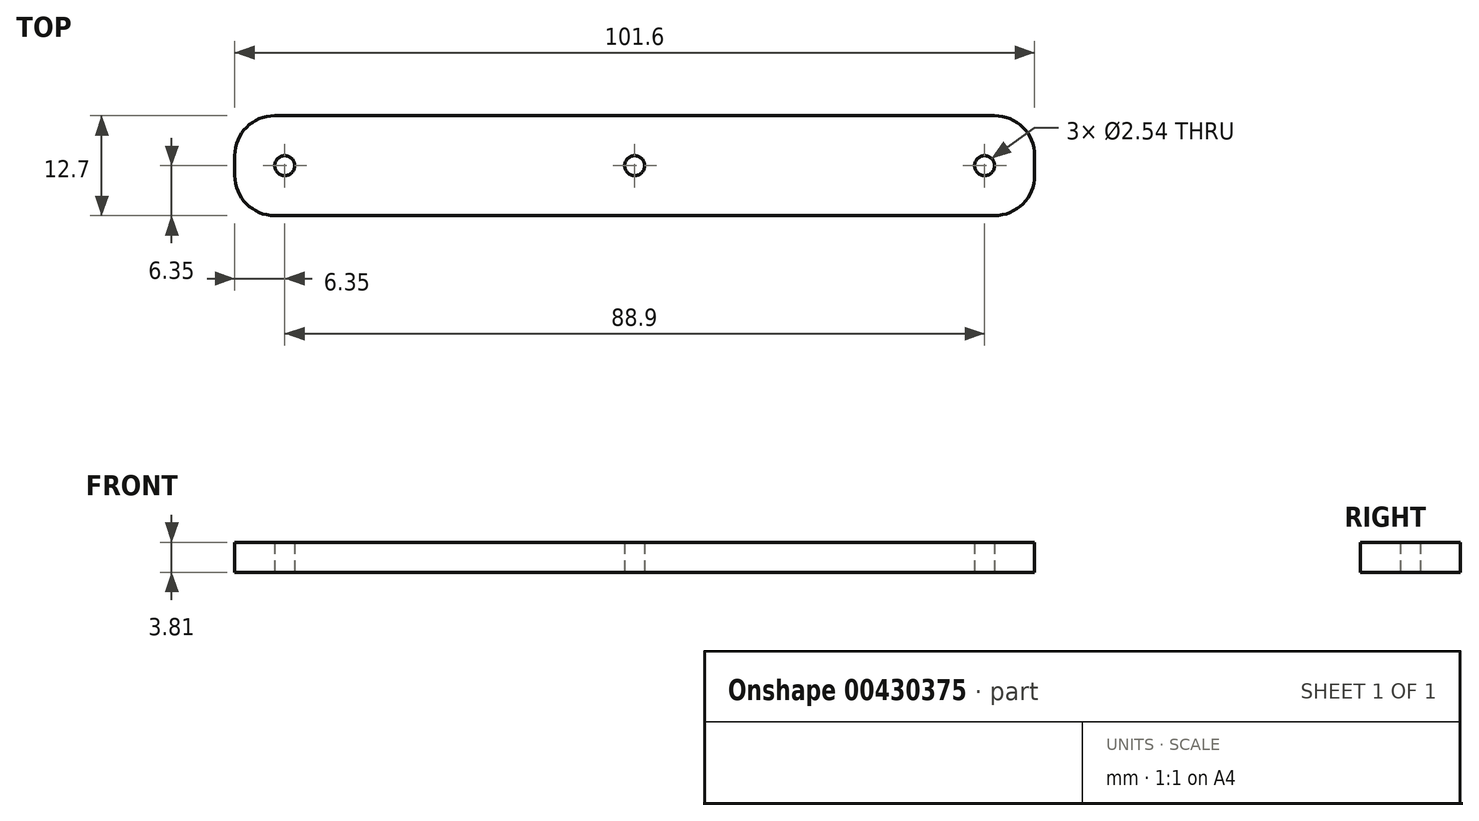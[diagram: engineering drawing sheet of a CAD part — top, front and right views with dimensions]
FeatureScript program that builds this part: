
annotation { "Feature Type Name" : "Feature", "Feature Type Description" : "" }
export const myFeature = defineFeature(function(context is Context, id is Id, definition is map)
    precondition{}
    {
        {
            var Q0;
            Q0=qCreatedBy(makeId("Top.planeOp"),FACE);
            var sketch = newSketch(context, id + "F0", { "sketchPlane" : qUnion([Q0])});
            skLineSegment(sketch, "E0.bottom", {"start": v(0, 0) * mm, "end": v(-101.6, 0) * mm});
            skLineSegment(sketch, "E0.top", {"start": v(0, 12.7) * mm, "end": v(-101.6, 12.7) * mm});
            skLineSegment(sketch, "E0.left", {"start": v(0, 0) * mm, "end": v(0, 12.7) * mm});
            skLineSegment(sketch, "E0.right", {"start": v(-101.6, 0) * mm, "end": v(-101.6, 12.7) * mm});
            skCircle(sketch, "E1", {"center": v(-95.25, 6.35) * mm, "radius": 1.27 * mm});
            skCircle(sketch, "E2", {"center": v(-50.8, 6.35) * mm, "radius": 1.27 * mm});
            skCircle(sketch, "E3", {"center": v(-6.35, 6.35) * mm, "radius": 1.27 * mm});
            skSolve(sketch);
        }
        {
            var Q0;
            Q0=makeQuery(id+"F0.imprint","IMPRINT",FACE,{"disambiguationData":[TD([[makeQuery(id+"F0.imprint","IMPRINT",EDGE,{"derivedFrom":sQuery(id+"F0.wireOp",EDGE,"E0.bottom")}),-1.0]])]});
            extrude(context, id + "F1", {"entities" : qUnion([Q0]), "depth" : 3.8 * mm});
        }
        {
            var Q0;
            Q0=makeQuery(id+"F1.opExtrude","SWEPT_EDGE",EDGE,{"disambiguationData":[OSD([sQuery(id+"F0.wireOp",EDGE,"E0.bottom"),sQuery(id+"F0.wireOp",EDGE,"E0.left")])]});
            var Q1;
            Q1=makeQuery(id+"F1.opExtrude","SWEPT_EDGE",EDGE,{"disambiguationData":[OSD([sQuery(id+"F0.wireOp",EDGE,"E0.top"),sQuery(id+"F0.wireOp",EDGE,"E0.left")])]});
            var Q2;
            Q2=makeQuery(id+"F1.opExtrude","SWEPT_EDGE",EDGE,{"disambiguationData":[OSD([sQuery(id+"F0.wireOp",EDGE,"E0.top"),sQuery(id+"F0.wireOp",EDGE,"E0.right")])]});
            var Q3;
            Q3=makeQuery(id+"F1.opExtrude","SWEPT_EDGE",EDGE,{"disambiguationData":[OSD([sQuery(id+"F0.wireOp",EDGE,"E0.bottom"),sQuery(id+"F0.wireOp",EDGE,"E0.right")])]});
            fillet(context, id + "F2", {"entities" : qUnion([Q0, Q1, Q2, Q3]), "radius" : 5.08 * mm, "tangentPropagation" : true, "allowEdgeOverflow" : false});
        }
    });
